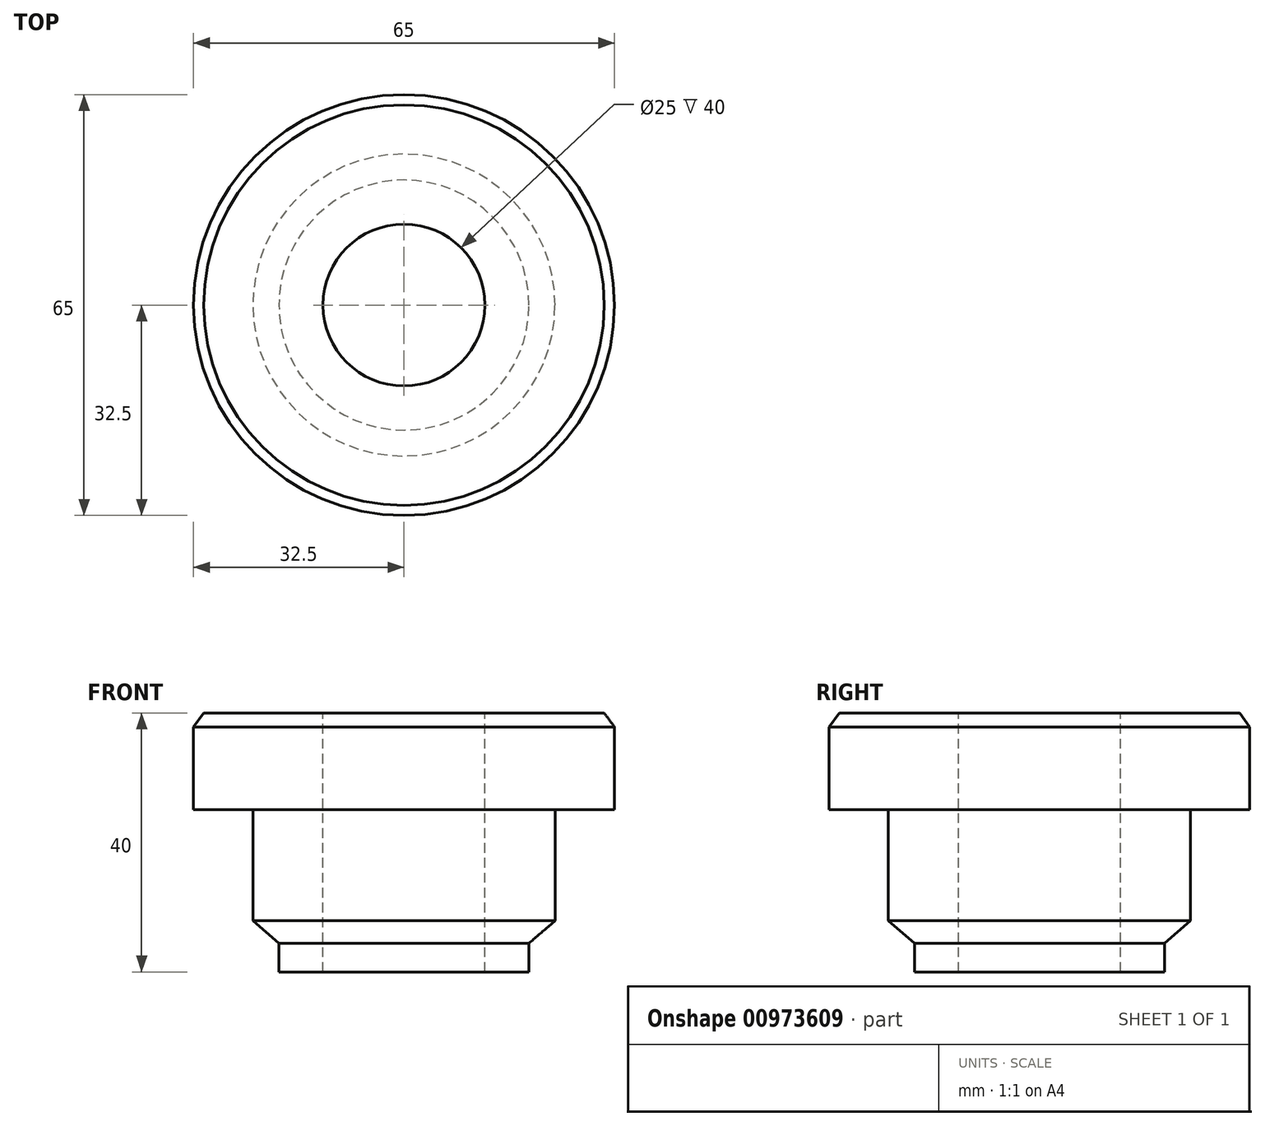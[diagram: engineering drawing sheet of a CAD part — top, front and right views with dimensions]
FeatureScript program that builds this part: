
annotation { "Feature Type Name" : "Feature", "Feature Type Description" : "" }
export const myFeature = defineFeature(function(context is Context, id is Id, definition is map)
    precondition{}
    {
        {
            var Q0;
            Q0=qCreatedBy(makeId("Front.planeOp"),FACE);
            var sketch = newSketch(context, id + "F0", { "sketchPlane" : qUnion([Q0])});
            skLineSegment(sketch, "E0", {"start": v(0, 0) * mm, "end": v(0, 4.44) * mm});
            skLineSegment(sketch, "E1", {"start": v(0, 4.44) * mm, "end": v(4.01, 7.89) * mm});
            skLineSegment(sketch, "E2", {"start": v(4.01, 7.89) * mm, "end": v(4.01, 25.09) * mm});
            skLineSegment(sketch, "E3", {"start": v(4.01, 25.09) * mm, "end": v(13.19, 25.09) * mm});
            skLineSegment(sketch, "E4", {"start": v(13.19, 25.09) * mm, "end": v(13.19, 37.85) * mm});
            skLineSegment(sketch, "E5", {"start": v(13.19, 37.85) * mm, "end": v(11.61, 40) * mm});
            skLineSegment(sketch, "E6", {"start": v(11.61, 40) * mm, "end": v(-19.31, 40) * mm});
            skLineSegment(sketch, "E7", {"start": v(-19.31, 40) * mm, "end": v(-19.31, 0) * mm});
            skLineSegment(sketch, "E8", {"start": v(-19.31, 0) * mm, "end": v(0, 0) * mm});
            skSolve(sketch);
        }
        {
            var Q0;
            Q0=makeQuery(id+"F0.imprint","IMPRINT",FACE,{"disambiguationData":[TD([[makeQuery(id+"F0.imprint","IMPRINT",EDGE,{"derivedFrom":sQuery(id+"F0.wireOp",EDGE,"E0")}),1.0]])]});
            var Q1;
            Q1=sQuery(id+"F0.wireOp",EDGE,"E7");
            revolve(context, id + "F1", {"surfaceOperationType" : NewSurfaceOperationType.NEW, "entities" : qUnion([Q0]), "axis" : qUnion([Q1]), "revolveType" : RevolveType.FULL});
        }
        {
            var Q0;
            Q0=makeQuery(id+"F1.opRevolve","SWEPT_FACE",FACE,{"disambiguationData":[OSD([sQuery(id+"F0.wireOp",EDGE,"E6")])]});
            var sketch = newSketch(context, id + "F2", { "sketchPlane" : qUnion([Q0])});
            skCircle(sketch, "E9", {"center": v(-19.31, 0) * mm, "radius": 12.5 * mm});
            skSolve(sketch);
        }
        {
            var Q0;
            Q0=qSketchRegion(id+"F2",true);
            extrude(context, id + "F3", {"entities" : qUnion([Q0]), "operationType" : NewBodyOperationType.REMOVE, "endBound" : BoundingType.THROUGH_ALL, "oppositeDirection" : true, "depth" : 25 * mm, "offsetDistance" : 25 * mm});
        }
    });
